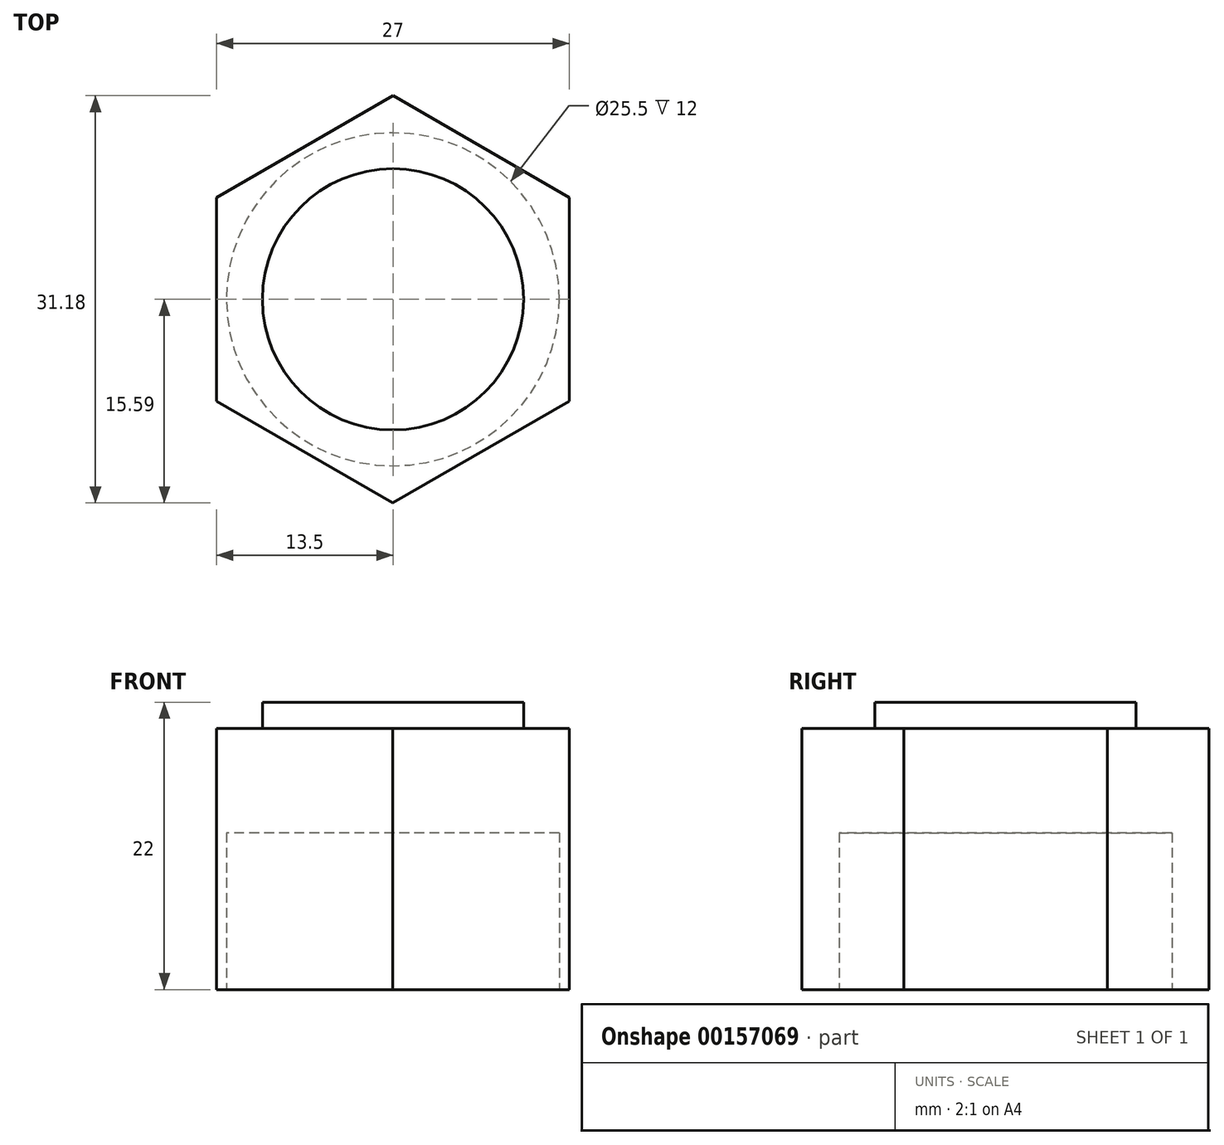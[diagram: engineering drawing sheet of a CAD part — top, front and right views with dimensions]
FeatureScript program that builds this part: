
annotation { "Feature Type Name" : "Feature", "Feature Type Description" : "" }
export const myFeature = defineFeature(function(context is Context, id is Id, definition is map)
    precondition{}
    {
        {
            var Q0;
            Q0=qCreatedBy(makeId("Top.planeOp"),FACE);
            var sketch = newSketch(context, id + "F0", { "sketchPlane" : qUnion([Q0])});
            skCircle(sketch, "E0.cCircle", {"center": v(0, 0) * mm, "radius": 13.5 * mm, "construction": true});
            skLineSegment(sketch, "E0.0", {"start": v(-13.5, 7.8) * mm, "end": v(0, 15.59) * mm});
            skLineSegment(sketch, "E0.1", {"start": v(0, 15.59) * mm, "end": v(13.5, 7.8) * mm});
            skLineSegment(sketch, "E0.2", {"start": v(13.5, 7.8) * mm, "end": v(13.5, -7.8) * mm});
            skLineSegment(sketch, "E0.3", {"start": v(13.5, -7.8) * mm, "end": v(0, -15.59) * mm});
            skLineSegment(sketch, "E0.4", {"start": v(0, -15.59) * mm, "end": v(-13.5, -7.8) * mm});
            skLineSegment(sketch, "E0.5", {"start": v(-13.5, -7.8) * mm, "end": v(-13.5, 7.8) * mm});
            skPoint(sketch, "E0.0.midPoint", {"position": v(-6.75, 11.7) * mm});
            skSolve(sketch);
        }
        {
            var Q0;
            Q0 = qSketchRegion(id + "F0", true);
            extrude(context, id + "F1", {"entities" : qUnion([Q0]), "depth" : 20 * mm});
        }
        {
            var Q0;
            Q0=qCreatedBy(makeId("Top.planeOp"),FACE);
            var sketch = newSketch(context, id + "F2", { "sketchPlane" : qUnion([Q0])});
            skCircle(sketch, "E1", {"center": v(0, 0) * mm, "radius": 12.75 * mm});
            skSolve(sketch);
        }
        {
            var Q0;
            Q0 = qSketchRegion(id + "F2", true);
            extrude(context, id + "F3", {"entities" : qUnion([Q0]), "operationType" : NewBodyOperationType.REMOVE, "depth" : 12 * mm});
        }
        {
            var Q0;
            Q0=makeQuery(id+"F1.opExtrude","CAP_FACE",FACE,{"disambiguationData":[OSD([sQuery(id+"F0.wireOp",EDGE,"E0.0"),sQuery(id+"F0.wireOp",EDGE,"E0.1"),sQuery(id+"F0.wireOp",EDGE,"E0.2"),sQuery(id+"F0.wireOp",EDGE,"E0.3"),sQuery(id+"F0.wireOp",EDGE,"E0.4"),sQuery(id+"F0.wireOp",EDGE,"E0.5")])],"isStart":false});
            var sketch = newSketch(context, id + "F4", { "sketchPlane" : qUnion([Q0])});
            skCircle(sketch, "E2", {"center": v(0, 0) * mm, "radius": 10 * mm});
            skSolve(sketch);
        }
        {
            var Q0;
            Q0 = qSketchRegion(id + "F4", true);
            extrude(context, id + "F5", {"entities" : qUnion([Q0]), "operationType" : NewBodyOperationType.ADD, "depth" : 2 * mm});
        }
    });
